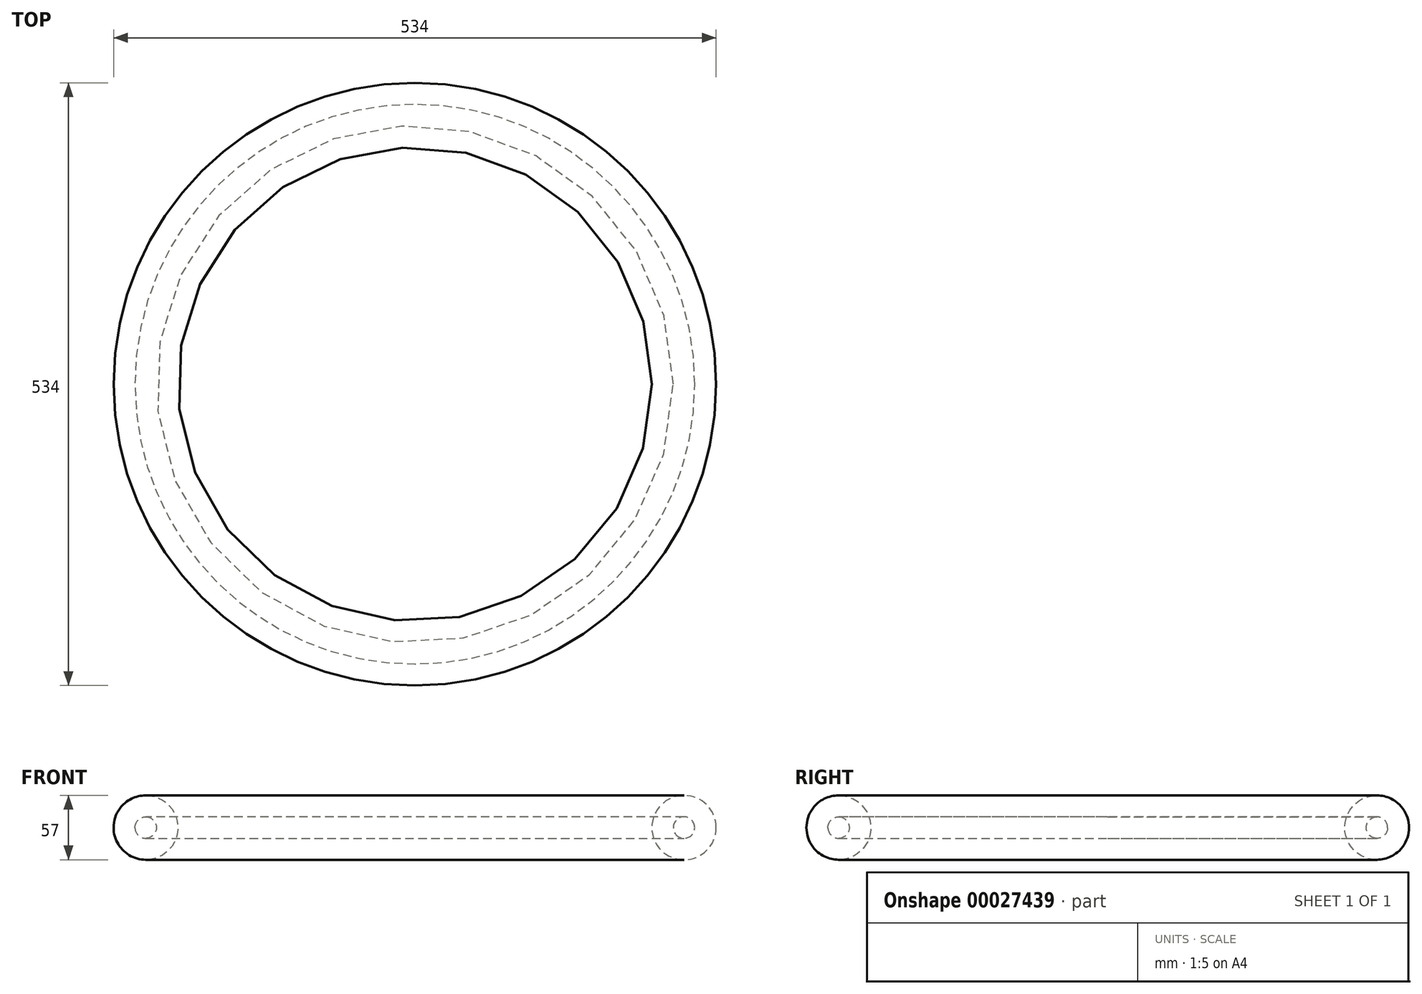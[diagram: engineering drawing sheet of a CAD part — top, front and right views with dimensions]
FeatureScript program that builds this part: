
annotation { "Feature Type Name" : "Feature", "Feature Type Description" : "" }
export const myFeature = defineFeature(function(context is Context, id is Id, definition is map)
    precondition{}
    {
        {
            var Q0;
            Q0=qCreatedBy(makeId("Front.planeOp"),FACE);
            var sketch = newSketch(context, id + "F0", { "sketchPlane" : qUnion([Q0])});
            skCircle(sketch, "E0", {"center": v(238.5, 0) * mm, "radius": 28.5 * mm});
            skLineSegment(sketch, "E1", {"start": v(0, 0) * mm, "end": v(210, 0) * mm});
            skLineSegment(sketch, "E2", {"start": v(0, 74.76) * mm, "end": v(0, -74.62) * mm});
            skCircle(sketch, "E3", {"center": v(238.5, 0) * mm, "radius": 9.5 * mm});
            skSolve(sketch);
        }
        {
            var Q0;
            Q0=makeQuery(id+"F0.imprint","IMPRINT",FACE,{"disambiguationData":[TD([[makeQuery(id+"F0.imprint","IMPRINT",EDGE,{"derivedFrom":sQuery(id+"F0.wireOp",EDGE,"E0")}),1.0]])]});
            var Q1;
            Q1=sQuery(id+"F0.wireOp",EDGE,"E2");
            revolve(context, id + "F1", {"entities" : qUnion([Q0]), "axis" : qUnion([Q1]), "revolveType" : RevolveType.FULL});
        }
    });
